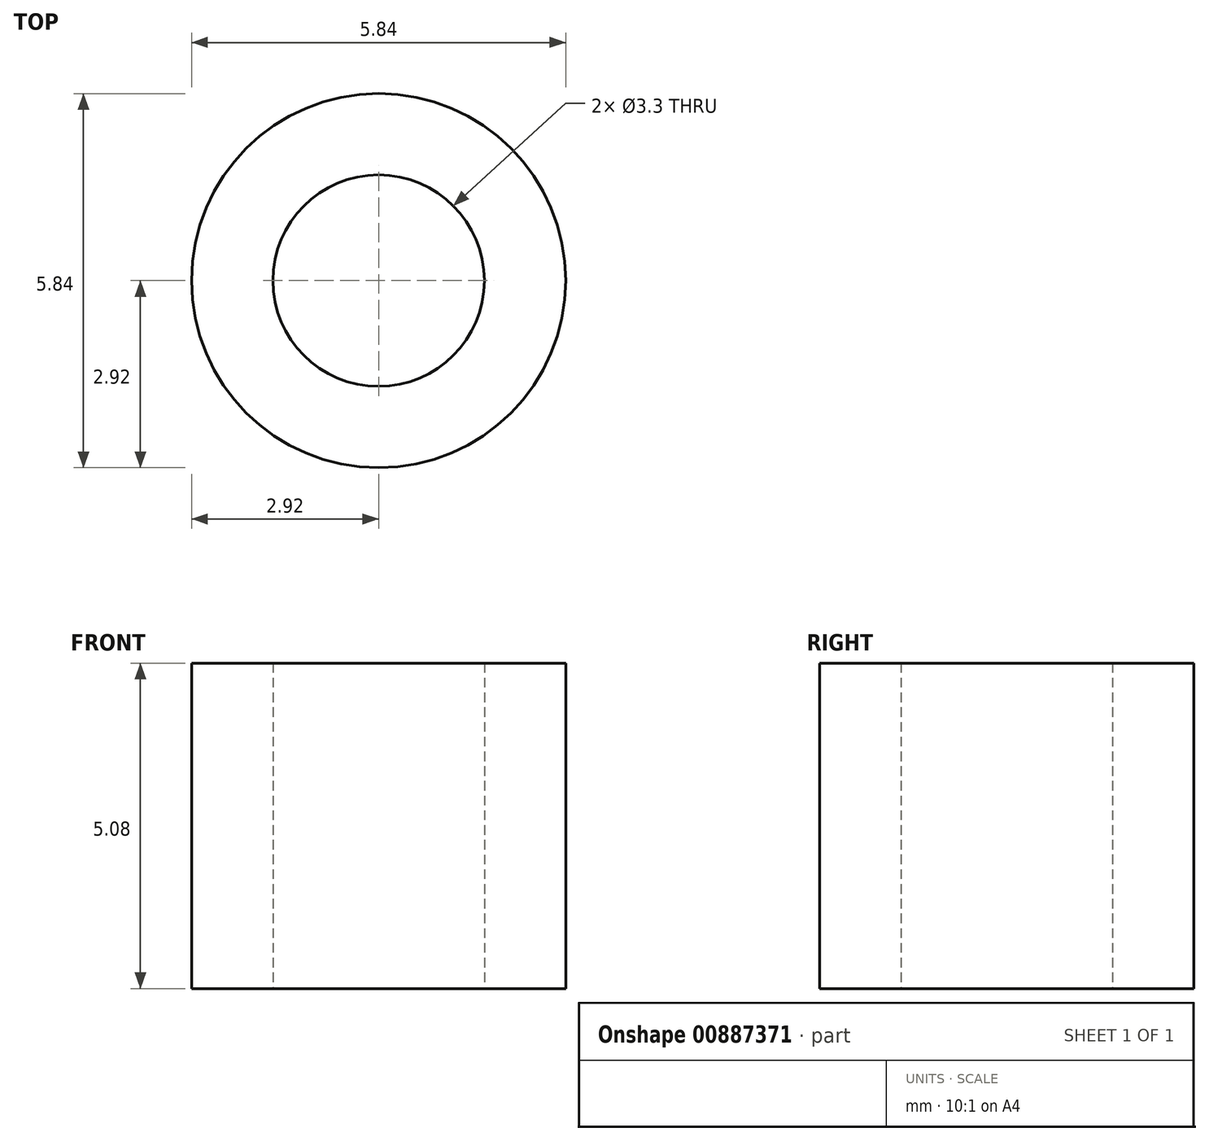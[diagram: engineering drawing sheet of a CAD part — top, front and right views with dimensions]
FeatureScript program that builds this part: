
annotation { "Feature Type Name" : "Feature", "Feature Type Description" : "" }
export const myFeature = defineFeature(function(context is Context, id is Id, definition is map)
    precondition{}
    {
        {
            var Q0;
            Q0=qCreatedBy(makeId("Top.planeOp"),FACE);
            var sketch = newSketch(context, id + "F0", { "sketchPlane" : qUnion([Q0])});
            skCircle(sketch, "E0", {"center": v(0, 0) * mm, "radius": 1.65 * mm});
            skCircle(sketch, "E1", {"center": v(0, 0) * mm, "radius": 2.92 * mm});
            skSolve(sketch);
        }
        {
            var Q0;
            Q0 = qSketchRegion(id + "F0", true);
            extrude(context, id + "F1", {"entities" : qUnion([Q0]), "depth" : 5.08 * mm, "offsetDistance" : 25.4 * mm});
        }
    });
